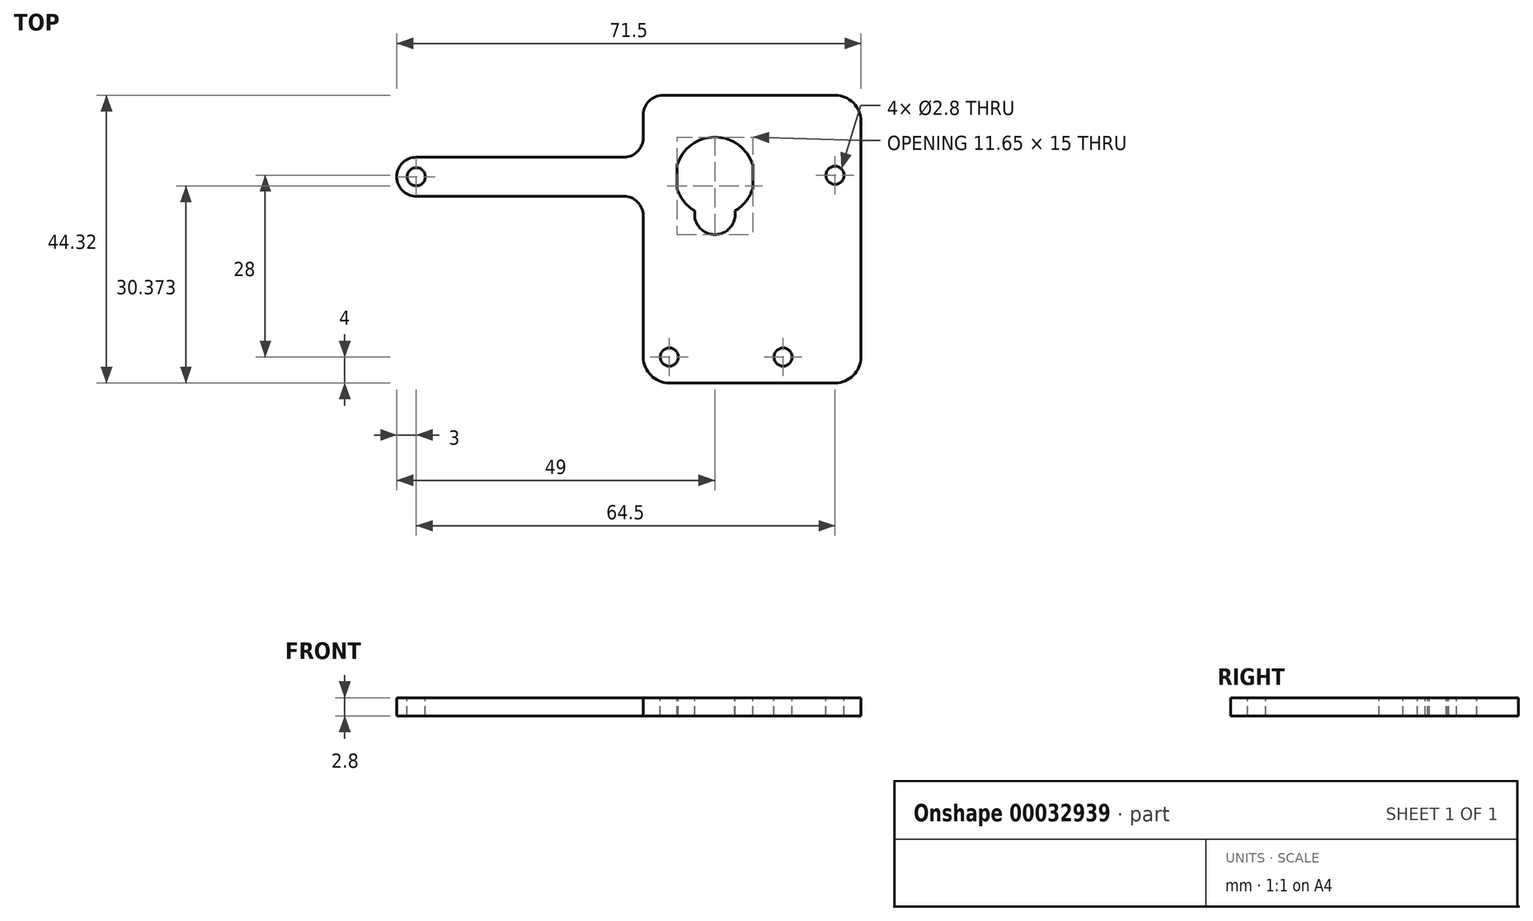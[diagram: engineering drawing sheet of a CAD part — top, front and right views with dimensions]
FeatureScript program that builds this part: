
annotation { "Feature Type Name" : "Feature", "Feature Type Description" : "" }
export const myFeature = defineFeature(function(context is Context, id is Id, definition is map)
    precondition{}
    {
        {
            var Q0;
            Q0=qCreatedBy(makeId("Top.planeOp"),FACE);
            var sketch = newSketch(context, id + "F0", { "sketchPlane" : qUnion([Q0])});
            skLineSegment(sketch, "E0.rect.bottom", {"start": v(5.82, -11.88) * mm, "end": v(-5.83, -11.88) * mm});
            skLineSegment(sketch, "E0.rect.top", {"start": v(5.83, 11.88) * mm, "end": v(-5.82, 11.88) * mm});
            skLineSegment(sketch, "E0.rect.left", {"start": v(5.82, -11.88) * mm, "end": v(5.83, 11.88) * mm});
            skLineSegment(sketch, "E0.rect.right", {"start": v(-5.83, -11.88) * mm, "end": v(-5.82, 11.87) * mm});
            skPoint(sketch, "E0.rect.middle", {"position": v(0, 0) * mm});
            skSolve(sketch);
        }
        {
            var Q0;
            Q0=qSketchRegion(id+"F0",true);
            extrude(context, id + "F1", {"entities" : qUnion([Q0]), "depth" : 20.4 * mm});
        }
        {
            var Q0;
            Q0=makeQuery(id+"F1.opExtrude","CAP_FACE",FACE,{"disambiguationData":[OSD([sQuery(id+"F0.wireOp",EDGE,"E0.rect.bottom"),sQuery(id+"F0.wireOp",EDGE,"E0.rect.top"),sQuery(id+"F0.wireOp",EDGE,"E0.rect.left"),sQuery(id+"F0.wireOp",EDGE,"E0.rect.right")])],"isStart":false});
            var sketch = newSketch(context, id + "F2", { "sketchPlane" : qUnion([Q0])});
            skArc(sketch, "E1", {"start": v(5.83, 7.59) * mm, "mid": v(0, 11.88) * mm, "end": v(-5.83, 7.59) * mm});
            skLineSegment(sketch, "E2", {"start": v(5.83, 7.59) * mm, "end": v(5.83, 3.96) * mm});
            skLineSegment(sketch, "E3.MirrorCS", {"start": v(-5.83, 7.59) * mm, "end": v(-5.83, 3.96) * mm});
            skArc(sketch, "E4.trimOffspring", {"start": v(-5.83, 3.96) * mm, "mid": v(-4.78, 1.98) * mm, "end": v(-3.09, 0.51) * mm});
            skArc(sketch, "E5", {"start": v(-3.09, 0.51) * mm, "mid": v(0, -3.1) * mm, "end": v(3.09, 0.51) * mm});
            skArc(sketch, "E6.trimOffspring", {"start": v(3.09, 0.51) * mm, "mid": v(4.78, 1.98) * mm, "end": v(5.83, 3.96) * mm});
            skSolve(sketch);
        }
        {
            var Q0;
            Q0=qSketchRegion(id+"F2",true);
            extrude(context, id + "F3", {"entities" : qUnion([Q0]), "operationType" : NewBodyOperationType.ADD, "depth" : 6 * mm});
        }
        {
            var Q0;
            {var subQ0=sQuery(id+"F0.wireOp",EDGE,"E0.rect.bottom");var subQ1=sQuery(id+"F0.wireOp",EDGE,"E0.rect.left");var subQ2=sQuery(id+"F0.wireOp",EDGE,"E0.rect.right");Q0=makeQuery(id+"F3.boolean.opBoolean","SPLIT",FACE,{"disambiguationData":[TD([makeQuery(id+"F1.opExtrude","SWEPT_FACE",FACE,{"disambiguationData":[OSD([subQ0])]}),makeQuery(id+"F1.opExtrude","SWEPT_FACE",FACE,{"disambiguationData":[OSD([subQ1])]}),makeQuery(id+"F1.opExtrude","SWEPT_FACE",FACE,{"disambiguationData":[OSD([subQ2])]}),makeQuery(id+"F3.opExtrude","SWEPT_FACE",FACE,{"disambiguationData":[OSD([sQuery(id+"F2.wireOp",EDGE,"E2")])]}),makeQuery(id+"F3.opExtrude","SWEPT_FACE",FACE,{"disambiguationData":[OSD([sQuery(id+"F2.wireOp",EDGE,"E3.MirrorCS")])]}),makeQuery(id+"F3.opExtrude","SWEPT_FACE",FACE,{"disambiguationData":[OSD([sQuery(id+"F2.wireOp",EDGE,"E4.trimOffspring")])]}),makeQuery(id+"F3.opExtrude","SWEPT_FACE",FACE,{"disambiguationData":[OSD([sQuery(id+"F2.wireOp",EDGE,"E5")])]}),makeQuery(id+"F3.opExtrude","SWEPT_FACE",FACE,{"disambiguationData":[OSD([sQuery(id+"F2.wireOp",EDGE,"E6.trimOffspring")])]})])],"derivedFrom":makeQuery(id+"F1.opExtrude","CAP_FACE",FACE,{"disambiguationData":[OSD([subQ0,sQuery(id+"F0.wireOp",EDGE,"E0.rect.top"),subQ1,subQ2])],"isStart":false})});}
            var sketch = newSketch(context, id + "F4", { "sketchPlane" : qUnion([Q0])});
            skLineSegment(sketch, "E7.bottom", {"start": v(-5.83, -11.88) * mm, "end": v(5.82, -11.88) * mm});
            skLineSegment(sketch, "E7.top", {"start": v(-5.83, -16.08) * mm, "end": v(5.82, -16.08) * mm});
            skLineSegment(sketch, "E7.left", {"start": v(-5.83, -11.88) * mm, "end": v(-5.83, -16.08) * mm});
            skLineSegment(sketch, "E7.right", {"start": v(5.82, -11.88) * mm, "end": v(5.82, -16.08) * mm});
            skLineSegment(sketch, "E8.MirrorCS", {"start": v(-5.83, 11.88) * mm, "end": v(-5.83, 16.08) * mm});
            skLineSegment(sketch, "E9.MirrorCS", {"start": v(-5.83, 16.08) * mm, "end": v(5.82, 16.08) * mm});
            skLineSegment(sketch, "E10.MirrorCS", {"start": v(5.82, 11.88) * mm, "end": v(5.82, 16.08) * mm});
            skLineSegment(sketch, "E11.MirrorCS", {"start": v(-5.83, 11.88) * mm, "end": v(5.82, 11.88) * mm});
            skSolve(sketch);
        }
        {
            var Q0;
            Q0=makeQuery(id+"F4.imprint","IMPRINT",FACE,{"disambiguationData":[TD([[makeQuery(id+"F4.imprint","IMPRINT",EDGE,{"derivedFrom":sQuery(id+"F4.wireOp",EDGE,"E7.bottom")}),1.0]])]});
            var Q1;
            Q1=makeQuery(id+"F4.imprint","IMPRINT",FACE,{"disambiguationData":[TD([[makeQuery(id+"F4.imprint","IMPRINT",EDGE,{"derivedFrom":sQuery(id+"F4.wireOp",EDGE,"E8.MirrorCS")}),-1.0]])]});
            extrude(context, id + "F5", {"entities" : qUnion([Q0, Q1]), "operationType" : NewBodyOperationType.ADD, "oppositeDirection" : true, "depth" : 2.8 * mm, "hasSecondDirection" : true, "secondDirectionOppositeDirection" : true, "secondDirectionDepth" : .8 * mm});
        }
        {
            var Q0;
            {var subQ0=sQuery(id+"F0.wireOp",EDGE,"E0.rect.top");var subQ1=sQuery(id+"F0.wireOp",EDGE,"E0.rect.left");Q0=makeQuery(id+"F5.boolean.opBoolean","SPLIT",EDGE,{"disambiguationData":[TD([makeQuery(id+"F1.opExtrude","CAP_FACE",FACE,{"disambiguationData":[OSD([sQuery(id+"F0.wireOp",EDGE,"E0.rect.bottom"),subQ0,subQ1,sQuery(id+"F0.wireOp",EDGE,"E0.rect.right")])],"isStart":true})])],"derivedFrom":makeQuery(id+"F1.opExtrude","SWEPT_EDGE",EDGE,{"disambiguationData":[OSD([subQ0,subQ1])]})});}
            var Q1;
            {var subQ0=sQuery(id+"F0.wireOp",EDGE,"E0.rect.bottom");var subQ1=sQuery(id+"F0.wireOp",EDGE,"E0.rect.left");Q1=makeQuery(id+"F5.boolean.opBoolean","SPLIT",EDGE,{"disambiguationData":[TD([makeQuery(id+"F1.opExtrude","CAP_FACE",FACE,{"disambiguationData":[OSD([subQ0,sQuery(id+"F0.wireOp",EDGE,"E0.rect.top"),subQ1,sQuery(id+"F0.wireOp",EDGE,"E0.rect.right")])],"isStart":true})])],"derivedFrom":makeQuery(id+"F1.opExtrude","SWEPT_EDGE",EDGE,{"disambiguationData":[OSD([subQ0,subQ1])]})});}
            var Q2;
            {var subQ0=sQuery(id+"F0.wireOp",EDGE,"E0.rect.bottom");var subQ1=sQuery(id+"F0.wireOp",EDGE,"E0.rect.right");Q2=makeQuery(id+"F5.boolean.opBoolean","SPLIT",EDGE,{"disambiguationData":[TD([makeQuery(id+"F1.opExtrude","CAP_FACE",FACE,{"disambiguationData":[OSD([subQ0,sQuery(id+"F0.wireOp",EDGE,"E0.rect.top"),sQuery(id+"F0.wireOp",EDGE,"E0.rect.left"),subQ1])],"isStart":true})])],"derivedFrom":makeQuery(id+"F1.opExtrude","SWEPT_EDGE",EDGE,{"disambiguationData":[OSD([subQ0,subQ1])]})});}
            var Q3;
            {var subQ0=sQuery(id+"F0.wireOp",EDGE,"E0.rect.top");var subQ1=sQuery(id+"F0.wireOp",EDGE,"E0.rect.right");Q3=makeQuery(id+"F5.boolean.opBoolean","SPLIT",EDGE,{"disambiguationData":[TD([makeQuery(id+"F1.opExtrude","CAP_FACE",FACE,{"disambiguationData":[OSD([sQuery(id+"F0.wireOp",EDGE,"E0.rect.bottom"),subQ0,sQuery(id+"F0.wireOp",EDGE,"E0.rect.left"),subQ1])],"isStart":true})])],"derivedFrom":makeQuery(id+"F1.opExtrude","SWEPT_EDGE",EDGE,{"disambiguationData":[OSD([subQ0,subQ1])]})});}
            fillet(context, id + "F6", {"entities" : qUnion([Q0, Q1, Q2, Q3]), "radius" : .5 * mm, "tangentPropagation" : true, "allowEdgeOverflow" : false});
        }
        {
            var Q0;
            Q0=makeQuery(id+"F5.opExtrude","SWEPT_EDGE",EDGE,{"disambiguationData":[OSD([sQuery(id+"F4.wireOp",EDGE,"E8.MirrorCS"),sQuery(id+"F4.wireOp",EDGE,"E9.MirrorCS")])]});
            var Q1;
            Q1=makeQuery(id+"F5.opExtrude","SWEPT_EDGE",EDGE,{"disambiguationData":[OSD([sQuery(id+"F4.wireOp",EDGE,"E9.MirrorCS"),sQuery(id+"F4.wireOp",EDGE,"E10.MirrorCS")])]});
            var Q2;
            Q2=makeQuery(id+"F5.opExtrude","SWEPT_EDGE",EDGE,{"disambiguationData":[OSD([sQuery(id+"F4.wireOp",EDGE,"E7.top"),sQuery(id+"F4.wireOp",EDGE,"E7.right")])]});
            var Q3;
            Q3=makeQuery(id+"F5.opExtrude","SWEPT_EDGE",EDGE,{"disambiguationData":[OSD([sQuery(id+"F4.wireOp",EDGE,"E7.top"),sQuery(id+"F4.wireOp",EDGE,"E7.left")])]});
            fillet(context, id + "F7", {"entities" : qUnion([Q0, Q1, Q2, Q3]), "radius" : 1 * mm, "tangentPropagation" : true, "allowEdgeOverflow" : false});
        }
        {
            var Q0;
            Q0=makeQuery(id+"F3.opExtrude","CAP_FACE",FACE,{"disambiguationData":[OSD([sQuery(id+"F2.wireOp",EDGE,"E1"),sQuery(id+"F2.wireOp",EDGE,"E2"),sQuery(id+"F2.wireOp",EDGE,"E3.MirrorCS"),sQuery(id+"F2.wireOp",EDGE,"E4.trimOffspring"),sQuery(id+"F2.wireOp",EDGE,"E5"),sQuery(id+"F2.wireOp",EDGE,"E6.trimOffspring")])],"isStart":false});
            var sketch = newSketch(context, id + "F8", { "sketchPlane" : qUnion([Q0])});
            skArc(sketch, "E12", {"start": v(3.09, 0.51) * mm, "mid": v(4.78, 1.98) * mm, "end": v(5.83, 3.96) * mm});
            skArc(sketch, "E13", {"start": v(-3.09, 0.51) * mm, "mid": v(0, -3.13) * mm, "end": v(3.09, 0.51) * mm});
            skLineSegment(sketch, "E14", {"start": v(-5.83, 3.96) * mm, "end": v(-5.83, 7.59) * mm});
            skLineSegment(sketch, "E15.MirrorCS", {"start": v(5.83, 3.96) * mm, "end": v(5.83, 7.59) * mm});
            skArc(sketch, "E16.trimOffspring", {"start": v(-5.83, 3.96) * mm, "mid": v(-4.78, 1.98) * mm, "end": v(-3.09, 0.51) * mm});
            skArc(sketch, "E17.trimOffspring", {"start": v(5.83, 7.59) * mm, "mid": v(0, 11.88) * mm, "end": v(-5.83, 7.59) * mm});
            skLineSegment(sketch, "E18.rect.left", {"start": v(22.5, 18.32) * mm, "end": v(22.5, -26) * mm});
            skLineSegment(sketch, "E19", {"start": v(1.61, 18.32) * mm, "end": v(-8.03, 18.32) * mm});
            skLineSegment(sketch, "E20", {"start": v(-11.03, 15.32) * mm, "end": v(-11.03, 11.78) * mm});
            skPoint(sketch, "E21.orphan", {"position": v(-22.5, 30) * mm});
            skPoint(sketch, "E22.visualSharp", {"position": v(-11.03, -26) * mm});
            skPoint(sketch, "E23.visualSharp", {"position": v(4.61, 18.32) * mm});
            skPoint(sketch, "E24.visualSharp", {"position": v(-11.03, 18.32) * mm});
            skArc(sketch, "E24.filletArc", {"start": v(-8.03, 18.32) * mm, "mid": v(-10.15, 17.44) * mm, "end": v(-11.03, 15.32) * mm});
            skLineSegment(sketch, "E25", {"start": v(0, 5.78) * mm, "end": v(-46, 5.78) * mm, "construction": true});
            skCircle(sketch, "E26", {"center": v(-46, 5.78) * mm, "radius": 1.4 * mm});
            skArc(sketch, "E27", {"start": v(-46, 8.78) * mm, "mid": v(-49, 5.78) * mm, "end": v(-46, 2.78) * mm});
            skLineSegment(sketch, "E28", {"start": v(-46, 2.78) * mm, "end": v(-14.03, 2.78) * mm});
            skLineSegment(sketch, "E29.MirrorCS", {"start": v(-46, 8.78) * mm, "end": v(-14.03, 8.78) * mm});
            skLineSegment(sketch, "E30.trimOffspring", {"start": v(-11.03, -0.22) * mm, "end": v(-11.03, -15.07) * mm});
            skPoint(sketch, "E31.visualSharp", {"position": v(-11.03, 8.78) * mm});
            skArc(sketch, "E31.filletArc", {"start": v(-14.03, 8.78) * mm, "mid": v(-11.9, 9.65) * mm, "end": v(-11.03, 11.78) * mm});
            skPoint(sketch, "E32.visualSharp", {"position": v(-11.03, 2.78) * mm});
            skArc(sketch, "E32.filletArc", {"start": v(-11.03, -0.22) * mm, "mid": v(-11.9, 1.9) * mm, "end": v(-14.03, 2.77) * mm});
            skLineSegment(sketch, "E33", {"start": v(-11.03, -15.07) * mm, "end": v(-11.03, -26) * mm});
            skLineSegment(sketch, "E34", {"start": v(-11.03, -26) * mm, "end": v(22.5, -26) * mm});
            skLineSegment(sketch, "E35.bottom", {"start": v(-11.03, -26) * mm, "end": v(-7.03, -26) * mm, "construction": true});
            skLineSegment(sketch, "E35.top", {"start": v(-11.03, -22) * mm, "end": v(-7.03, -22) * mm, "construction": true});
            skLineSegment(sketch, "E35.left", {"start": v(-11.03, -26) * mm, "end": v(-11.03, -22) * mm, "construction": true});
            skLineSegment(sketch, "E35.right", {"start": v(-7.03, -26) * mm, "end": v(-7.03, -22) * mm, "construction": true});
            skCircle(sketch, "E36", {"center": v(-7.03, -22) * mm, "radius": 1.4 * mm});
            skLineSegment(sketch, "E37.bottom", {"start": v(22.5, -26) * mm, "end": v(18.5, -26) * mm, "construction": true});
            skLineSegment(sketch, "E37.top", {"start": v(22.5, -22) * mm, "end": v(18.5, -22) * mm, "construction": true});
            skLineSegment(sketch, "E37.left", {"start": v(22.5, -26) * mm, "end": v(22.5, -22) * mm, "construction": true});
            skLineSegment(sketch, "E37.right", {"start": v(18.5, -26) * mm, "end": v(18.5, -22) * mm, "construction": true});
            skCircle(sketch, "E38", {"center": v(18.5, -22) * mm, "radius": 1.4 * mm, "construction": true});
            skLineSegment(sketch, "E39", {"start": v(1.61, 18.32) * mm, "end": v(22.5, 18.32) * mm});
            skCircle(sketch, "E40", {"center": v(18.5, 6) * mm, "radius": 1.4 * mm});
            skCircle(sketch, "E41", {"center": v(10.5, -22) * mm, "radius": 1.4 * mm});
            skSolve(sketch);
        }
        {
            var Q0;
            Q0=qSketchRegion(id+"F8",true);
            extrude(context, id + "F9", {"entities" : qUnion([Q0]), "oppositeDirection" : true, "depth" : 2.8 * mm});
        }
        {
            var Q0;
            Q0=makeQuery(id+"F9.opExtrude","SWEPT_EDGE",EDGE,{"disambiguationData":[OSD([sQuery(id+"F8.wireOp",EDGE,"E18.rect.top"),sQuery(id+"F8.wireOp",EDGE,"E18.rect.right")])]});
            var Q1;
            Q1=makeQuery(id+"F9.opExtrude","SWEPT_EDGE",EDGE,{"disambiguationData":[OSD([sQuery(id+"F8.wireOp",EDGE,"E18.rect.bottom"),sQuery(id+"F8.wireOp",EDGE,"E18.rect.right")])]});
            var Q2;
            Q2=makeQuery(id+"F9.opExtrude","SWEPT_EDGE",EDGE,{"disambiguationData":[OSD([sQuery(id+"F8.wireOp",EDGE,"E18.rect.bottom"),sQuery(id+"F8.wireOp",EDGE,"E18.rect.left")])]});
            var Q3;
            Q3=makeQuery(id+"F9.opExtrude","SWEPT_EDGE",EDGE,{"disambiguationData":[OSD([sQuery(id+"F8.wireOp",EDGE,"E18.rect.top"),sQuery(id+"F8.wireOp",EDGE,"E18.rect.left")])]});
            var Q4;
            Q4=makeQuery(id+"F9.opExtrude","SWEPT_EDGE",EDGE,{"disambiguationData":[OSD([sQuery(id+"F8.wireOp",EDGE,"E33"),sQuery(id+"F8.wireOp",EDGE,"E34")])]});
            fillet(context, id + "F10", {"entities" : qUnion([Q0, Q1, Q2, Q3, Q4]), "radius" : 4 * mm, "tangentPropagation" : true, "allowEdgeOverflow" : false});
        }
        {
            var Q0;
            Q0=makeQuery(id+"F9.opExtrude","SWEPT_BODY",BODY,{"disambiguationData":[OSD([sQuery(id+"F8.wireOp",EDGE,"E12"),sQuery(id+"F8.wireOp",EDGE,"E13"),sQuery(id+"F8.wireOp",EDGE,"E14"),sQuery(id+"F8.wireOp",EDGE,"E15.MirrorCS"),sQuery(id+"F8.wireOp",EDGE,"E16.trimOffspring"),sQuery(id+"F8.wireOp",EDGE,"E17.trimOffspring"),sQuery(id+"F8.wireOp",EDGE,"E18.rect.bottom"),sQuery(id+"F8.wireOp",EDGE,"E18.rect.top"),sQuery(id+"F8.wireOp",EDGE,"E18.rect.left"),sQuery(id+"F8.wireOp",EDGE,"E18.rect.right"),sQuery(id+"F8.wireOp",EDGE,"a12ce330-09d9-461c-8b2f-e163017ed208"),sQuery(id+"F8.wireOp",EDGE,"ce85554a-ae08-408d-bbdd-004999f886530.MirrorC"),sQuery(id+"F8.wireOp",EDGE,"74581e88-93ef-4e49-bf24-ccc966527bf30.MirrorC"),sQuery(id+"F8.wireOp",EDGE,"a9b9e684-8755-4f44-b45f-45d0958772250.MirrorC"),sQuery(id+"F8.wireOp",EDGE,"76930b9b-8da1-4d4d-b0e5-4a7641f42912"),sQuery(id+"F8.wireOp",EDGE,"f42893a9-d5a1-4c2e-96db-01520e8eb7290.MirrorC"),sQuery(id+"F8.wireOp",EDGE,"46118b25-6d7d-4224-8583-2d73bb83e9220.MirrorC"),sQuery(id+"F8.wireOp",EDGE,"b2e64fab-b84c-4731-9833-593c73ce0a330.MirrorC")])]});
            transform(context, id + "F11", {"entities" : qUnion([Q0]), "transformType" : TransformType.TRANSLATION_3D, "dx" : 0 * mm, "dy" : 0 * mm, "dz" : 0 * mm, "makeCopy" : true});
        }
        {
            var Q0;
            Q0=makeQuery(id+"F11.opPattern","COPY",BODY,{"derivedFrom":makeQuery(id+"F9.opExtrude","SWEPT_BODY",BODY,{"disambiguationData":[OSD([sQuery(id+"F8.wireOp",EDGE,"E12"),sQuery(id+"F8.wireOp",EDGE,"E13"),sQuery(id+"F8.wireOp",EDGE,"E14"),sQuery(id+"F8.wireOp",EDGE,"E15.MirrorCS"),sQuery(id+"F8.wireOp",EDGE,"E16.trimOffspring"),sQuery(id+"F8.wireOp",EDGE,"E17.trimOffspring"),sQuery(id+"F8.wireOp",EDGE,"E18.rect.bottom"),sQuery(id+"F8.wireOp",EDGE,"E18.rect.top"),sQuery(id+"F8.wireOp",EDGE,"E18.rect.left"),sQuery(id+"F8.wireOp",EDGE,"E18.rect.right"),sQuery(id+"F8.wireOp",EDGE,"a12ce330-09d9-461c-8b2f-e163017ed208"),sQuery(id+"F8.wireOp",EDGE,"74581e88-93ef-4e49-bf24-ccc966527bf30.MirrorC"),sQuery(id+"F8.wireOp",EDGE,"a9b9e684-8755-4f44-b45f-45d0958772250.MirrorC"),sQuery(id+"F8.wireOp",EDGE,"76930b9b-8da1-4d4d-b0e5-4a7641f42912"),sQuery(id+"F8.wireOp",EDGE,"f42893a9-d5a1-4c2e-96db-01520e8eb7290.MirrorC"),sQuery(id+"F8.wireOp",EDGE,"b2e64fab-b84c-4731-9833-593c73ce0a330.MirrorC"),sQuery(id+"F8.wireOp",EDGE,"6dbd4985-7d77-4368-82c7-85e426a01a06"),sQuery(id+"F8.wireOp",EDGE,"E19"),sQuery(id+"F8.wireOp",EDGE,"E20"),sQuery(id+"F8.wireOp",EDGE,"8f80475a-625c-4095-acb9-1eab8cfb7864"),sQuery(id+"F8.wireOp",EDGE,"E22.filletArc"),sQuery(id+"F8.wireOp",EDGE,"E23.filletArc"),sQuery(id+"F8.wireOp",EDGE,"E24.filletArc")])]}),"instanceName":"1"});
            deleteBodies(context, id + "F12", {"entities" : qUnion([Q0])});
        }
        {
            var Q0;
            Q0=makeQuery(id+"F1.opExtrude","SWEPT_BODY",BODY,{"disambiguationData":[OSD([sQuery(id+"F0.wireOp",EDGE,"E0.rect.bottom"),sQuery(id+"F0.wireOp",EDGE,"E0.rect.top"),sQuery(id+"F0.wireOp",EDGE,"E0.rect.left"),sQuery(id+"F0.wireOp",EDGE,"E0.rect.right")])]});
            deleteBodies(context, id + "F13", {"entities" : qUnion([Q0])});
        }
    });
